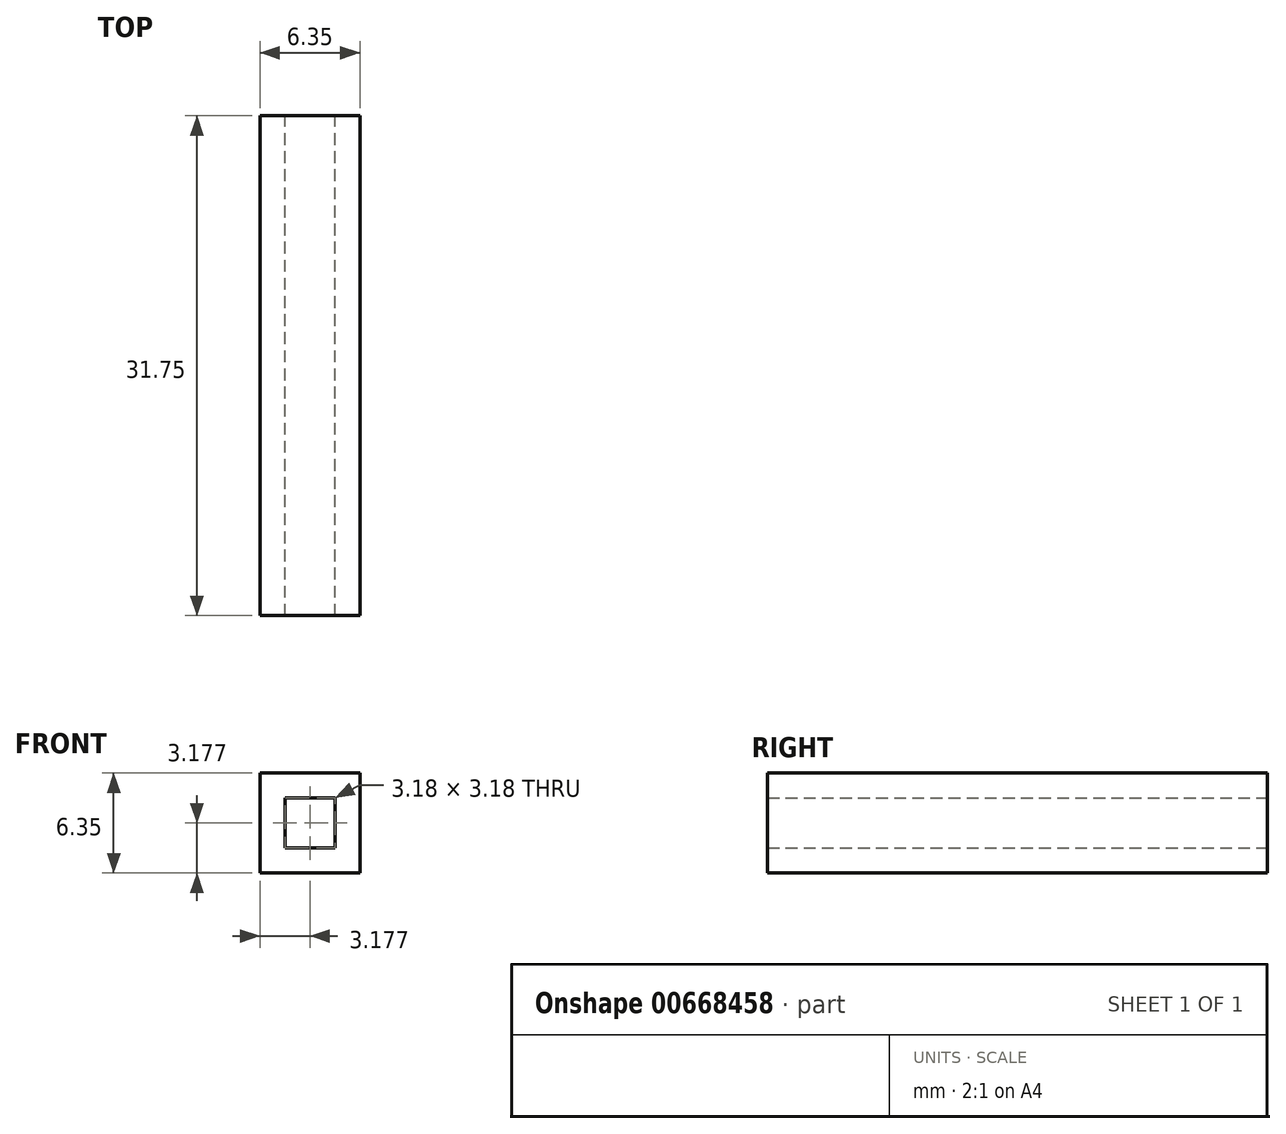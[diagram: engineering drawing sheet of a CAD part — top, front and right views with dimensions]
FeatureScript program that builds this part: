
annotation { "Feature Type Name" : "Feature", "Feature Type Description" : "" }
export const myFeature = defineFeature(function(context is Context, id is Id, definition is map)
    precondition{}
    {
        {
            var Q0;
            Q0=qCreatedBy(makeId("Front.planeOp"),FACE);
            var sketch = newSketch(context, id + "F0", { "sketchPlane" : qUnion([Q0])});
            skLineSegment(sketch, "E0.bottom", {"start": v(-12.7, 15.03) * mm, "end": v(-6.35, 15.03) * mm});
            skLineSegment(sketch, "E0.top", {"start": v(-12.7, 8.68) * mm, "end": v(-6.35, 8.68) * mm});
            skLineSegment(sketch, "E0.left", {"start": v(-12.7, 15.03) * mm, "end": v(-12.7, 8.68) * mm});
            skLineSegment(sketch, "E0.right", {"start": v(-6.35, 15.03) * mm, "end": v(-6.35, 8.68) * mm});
            skLineSegment(sketch, "E1.bottom", {"start": v(-11.11, 13.44) * mm, "end": v(-7.94, 13.44) * mm});
            skLineSegment(sketch, "E1.top", {"start": v(-11.11, 10.27) * mm, "end": v(-7.94, 10.27) * mm});
            skLineSegment(sketch, "E1.left", {"start": v(-11.11, 13.44) * mm, "end": v(-11.11, 10.27) * mm});
            skLineSegment(sketch, "E1.right", {"start": v(-7.94, 13.44) * mm, "end": v(-7.94, 10.27) * mm});
            skSolve(sketch);
        }
        {
            var Q0;
            Q0=makeQuery(id+"F0.imprint","IMPRINT",FACE,{"disambiguationData":[TD([[makeQuery(id+"F0.imprint","IMPRINT",EDGE,{"derivedFrom":sQuery(id+"F0.wireOp",EDGE,"E0.bottom")}),-1.0]])]});
            extrude(context, id + "F1", {"entities" : qUnion([Q0]), "depth" : 31.75 * mm});
        }
    });
